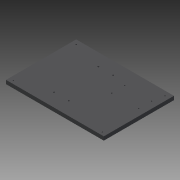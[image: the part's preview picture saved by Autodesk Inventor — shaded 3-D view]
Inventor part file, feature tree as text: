
AUTODESK INVENTOR PART (.ipt)
format: ipt  version: 2013 (Build 170138000, 138)  size: 115,712 bytes
history: native  units: mm
features: reference x6, sketch x4, hole x3, extrude x2
ambient origin geometry x8: Origin, YZ Plane, XZ Plane, XY Plane, X Axis, Y Axis, Z Axis, Center Point
bodies: Solid1 (feature_tree)
feature tree (15):
  extrude  "Extrusion1"  Depth=237.5mm
  extrude  "Extrusion2"  Depth=10.0mm TaperAngle=0.0deg
  hole  "Hole1"  [1 undecoded]
  hole  "Hole2"  [1 undecoded]
  hole  "Hole3"  [1 undecoded]
  sketch  "Sketch1"  dims[d0=331.0mm d2=237.5mm]
  sketch  "Sketch2"  dims[d3=12.5mm d4=0.0mm d5=10.0mm d6=0.0mm]
  reference  "Reference1"
  reference  "Reference2"
  reference  "Reference4"
  reference  "Reference5"
  sketch  "Sketch4"  dims[d7=6.5mm]
  reference  "Reference6"
  sketch  "Sketch5"  dims[d9=3.4mm d10=6.0mm d11=6.5mm d12=3.0mm d13=90.0deg d14=8.0mm d15=20.594885mm d16=4.5mm d17=6.0mm d18=8.0mm d19=4.0mm d20=90.0deg d21=8.0mm d22=20.594885mm d23=3.4mm d24=6.0mm d25=6.5mm d26=3.0mm d27=90.0deg d28=8.0mm d29=20.594885mm]
  reference  "Reference7"
note: 3 required parameter values undecoded (feature->parameter linkage not recoverable at this tier; creation-order binding heuristic only, values carry confidence <= 0.55)
